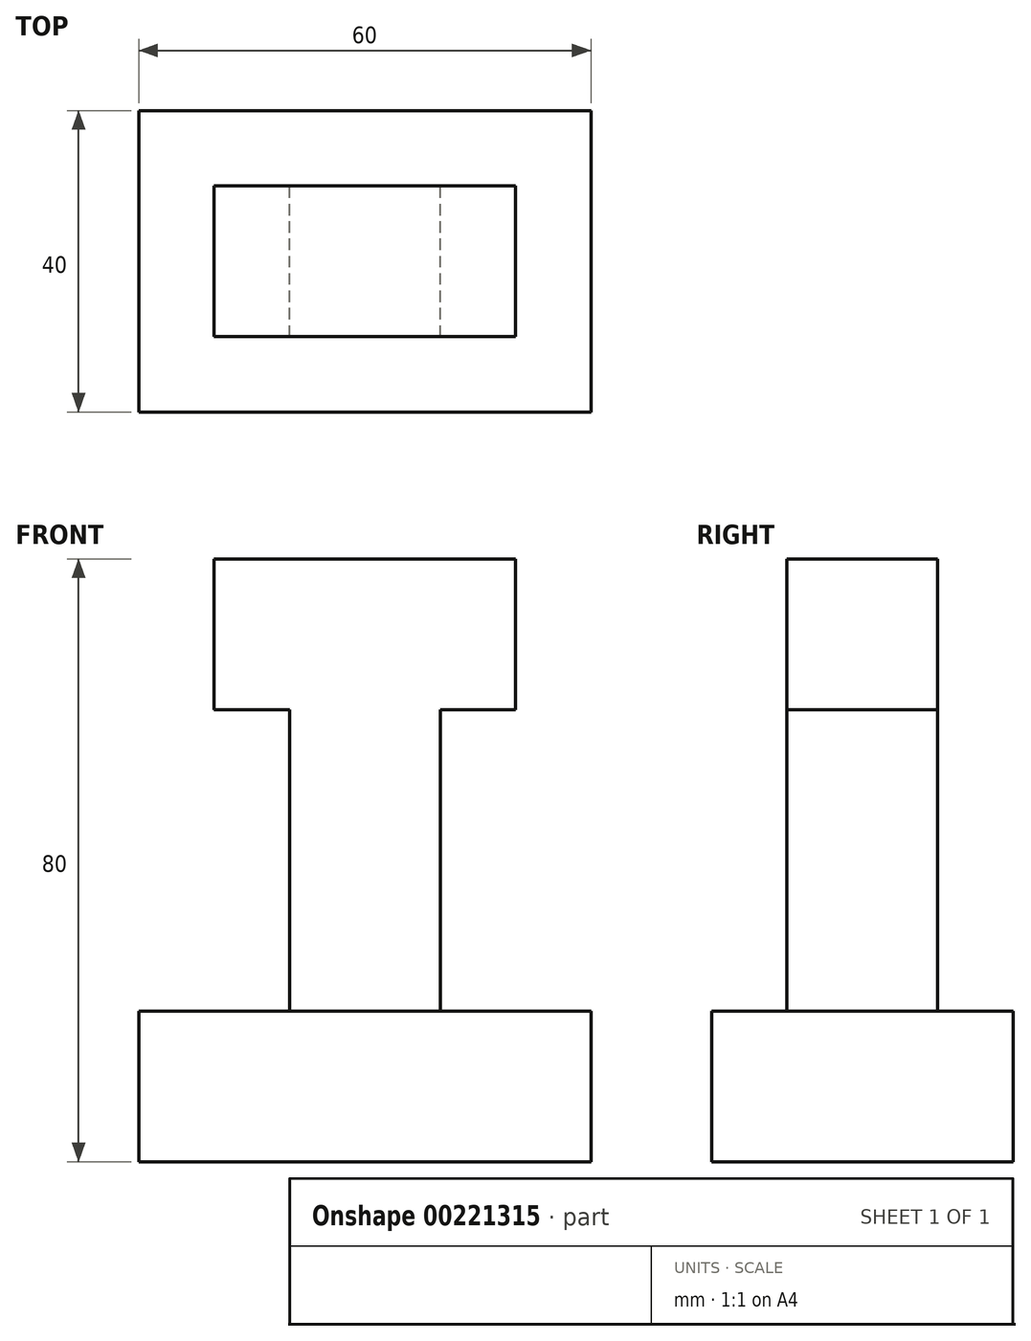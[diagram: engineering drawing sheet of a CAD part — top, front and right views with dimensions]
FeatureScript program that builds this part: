
annotation { "Feature Type Name" : "Feature", "Feature Type Description" : "" }
export const myFeature = defineFeature(function(context is Context, id is Id, definition is map)
    precondition{}
    {
        {
            var Q0;
            Q0=qCreatedBy(makeId("Front.planeOp"),FACE);
            var sketch = newSketch(context, id + "F0", { "sketchPlane" : qUnion([Q0])});
            skLineSegment(sketch, "E0", {"start": v(0, 0) * mm, "end": v(60, 0) * mm});
            skLineSegment(sketch, "E1", {"start": v(60, 0) * mm, "end": v(60, 20) * mm});
            skLineSegment(sketch, "E2", {"start": v(60, 20) * mm, "end": v(0, 20) * mm});
            skLineSegment(sketch, "E3", {"start": v(0, 20) * mm, "end": v(0, 0) * mm});
            skLineSegment(sketch, "E4", {"start": v(0, 0) * mm, "end": v(0, 0) * mm});
            skLineSegment(sketch, "E5", {"start": v(20, 20) * mm, "end": v(20, 60) * mm});
            skLineSegment(sketch, "E6", {"start": v(20, 60) * mm, "end": v(10, 60) * mm});
            skLineSegment(sketch, "E7", {"start": v(10, 60) * mm, "end": v(10, 80) * mm});
            skLineSegment(sketch, "E8", {"start": v(10, 80) * mm, "end": v(50, 80) * mm});
            skLineSegment(sketch, "E9", {"start": v(50, 80) * mm, "end": v(50, 60) * mm});
            skLineSegment(sketch, "E10", {"start": v(50, 60) * mm, "end": v(40, 60) * mm});
            skLineSegment(sketch, "E11", {"start": v(40, 60) * mm, "end": v(40, 20) * mm});
            skSolve(sketch);
        }
        {
            var Q0;
            Q0=makeQuery(id+"F0.imprint","IMPRINT",FACE,{"disambiguationData":[TD([[makeQuery(id+"F0.imprint","IMPRINT",EDGE,{"derivedFrom":sQuery(id+"F0.wireOp",EDGE,"E0")}),1.0]])]});
            extrude(context, id + "F1", {"entities" : qUnion([Q0]), "endBound" : BoundingType.SYMMETRIC, "depth" : 40 * mm});
        }
        {
            var Q0;
            {var subQ0=sQuery(id+"F0.wireOp",EDGE,"E5");Q0=makeQuery(id+"F0.imprint","IMPRINT",FACE,{"disambiguationData":[TD([[makeQuery(id+"F0.imprint","IMPRINT",EDGE,{"derivedFrom":subQ0}),-1.0]])]});}
            extrude(context, id + "F2", {"entities" : qUnion([Q0]), "operationType" : NewBodyOperationType.ADD, "endBound" : BoundingType.SYMMETRIC, "depth" : 20 * mm});
        }
    });
